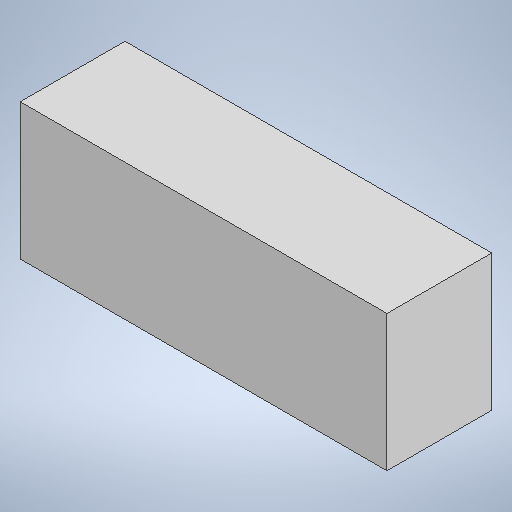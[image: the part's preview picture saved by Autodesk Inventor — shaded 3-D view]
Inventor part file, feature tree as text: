
AUTODESK INVENTOR PART (.ipt)
format: ipt  version: 2025 (Build 290162000, 162)  size: 182,272 bytes
history: native  units: mm
features: extrude x1, sketch x1
ambient origin geometry x8: Origin, YZ Plane, XZ Plane, XY Plane, X Axis, Y Axis, Z Axis, Center Point
bodies: Volumenkörper1 (feature_tree)
feature tree (2):
  extrude  "Extrusion1"  Depth=17.5mm
  sketch  "Skizze1"  dims[d0=6.5mm d1=17.5mm d2=5.0mm d3=0.0mm]
